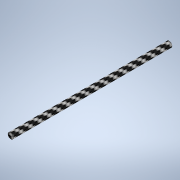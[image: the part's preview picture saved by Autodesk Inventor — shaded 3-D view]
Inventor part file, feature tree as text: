
AUTODESK INVENTOR PART (.ipt)
format: ipt  version: 2020 (Build 240168000, 168)  size: 108,032 bytes
history: native  units: in
note: dims shown in document units (in); Inventor stores cm internally (conversion verified against a paired STEP export)
features: extrude x1, sketch x1
ambient origin geometry x8: Origin, YZ Plane, XZ Plane, XY Plane, X Axis, Y Axis, Z Axis, Center Point
bodies: Solid1 (feature_tree)
feature tree (2):
  extrude  "Extrusion1"  Depth=2.4807in
  sketch  "Sketch1"  dims[d0=0.0906in d1=2.4807in d2=0.0in]
